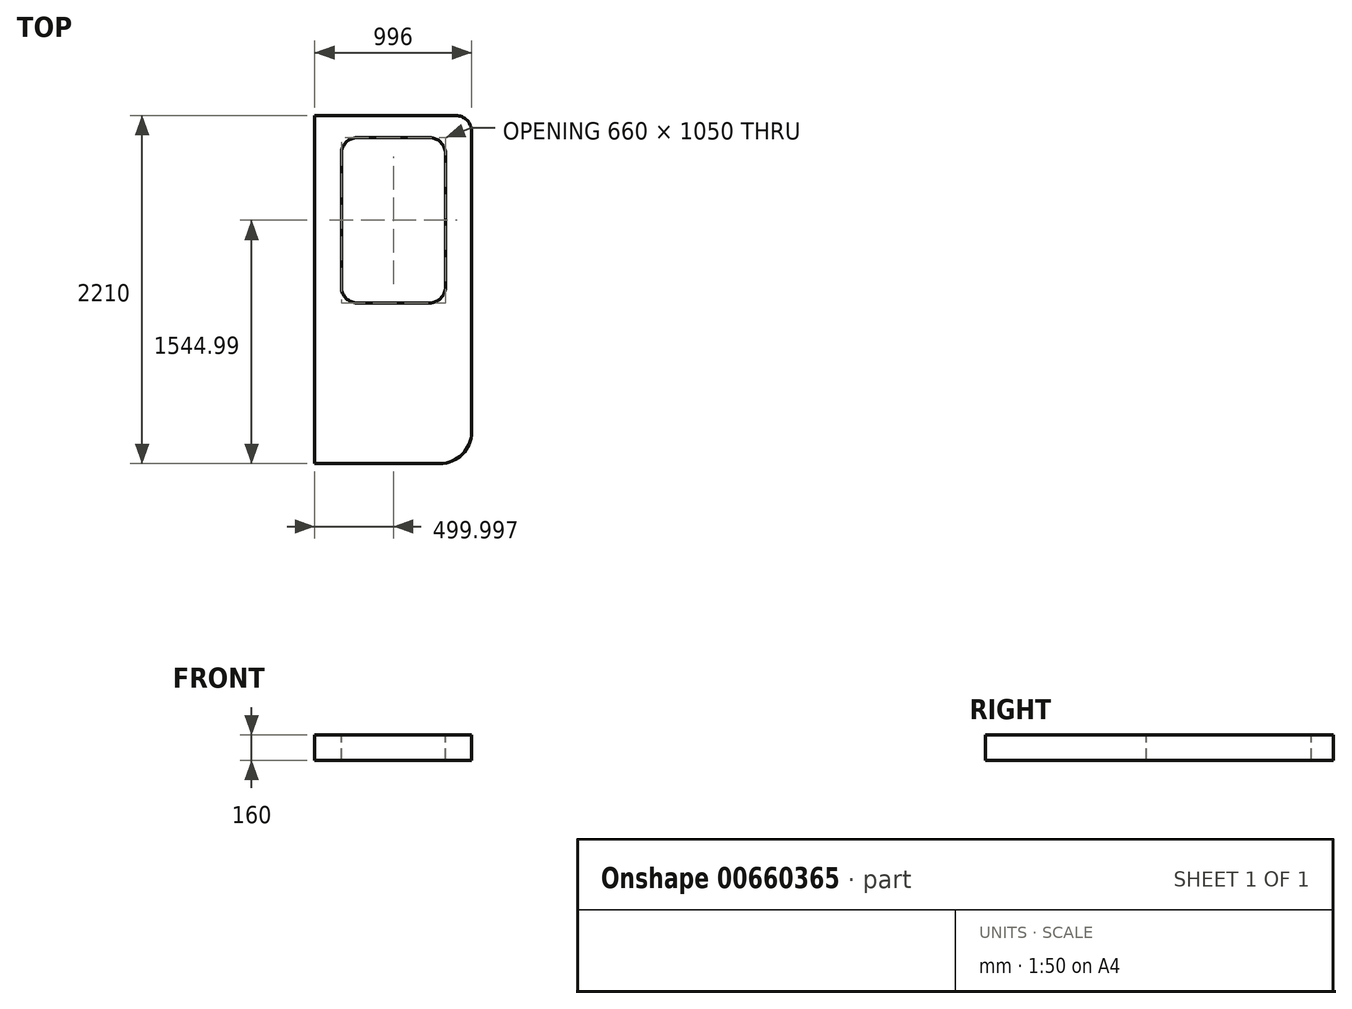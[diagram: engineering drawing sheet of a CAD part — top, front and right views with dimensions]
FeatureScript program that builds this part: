
annotation { "Feature Type Name" : "Feature", "Feature Type Description" : "" }
export const myFeature = defineFeature(function(context is Context, id is Id, definition is map)
    precondition{}
    {
        {
            var Q0;
            Q0=qCreatedBy(makeId("Top.planeOp"),FACE);
            var sketch = newSketch(context, id + "F0", { "sketchPlane" : qUnion([Q0])});
            skLineSegment(sketch, "E0.bottom", {"start": v(-58, 2153.08) * mm, "end": v(938, 2153.08) * mm});
            skLineSegment(sketch, "E0.top", {"start": v(-58, -56.92) * mm, "end": v(938, -56.92) * mm});
            skLineSegment(sketch, "E0.left", {"start": v(-58, 2153.08) * mm, "end": v(-58, -56.92) * mm});
            skLineSegment(sketch, "E0.right", {"start": v(938, 2153.08) * mm, "end": v(938, -56.92) * mm});
            skSolve(sketch);
        }
        {
            var Q0;
            Q0=makeQuery(id+"F0.imprint","IMPRINT",FACE,{"disambiguationData":[TD([[makeQuery(id+"F0.imprint","IMPRINT",EDGE,{"derivedFrom":sQuery(id+"F0.wireOp",EDGE,"E0.bottom")}),-1.0]])]});
            extrude(context, id + "F1", {"entities" : qUnion([Q0]), "depth" : 160 * mm, "offsetDistance" : 25 * mm});
        }
        {
            var Q0;
            Q0=makeQuery(id+"F1.opExtrude","SWEPT_EDGE",EDGE,{"disambiguationData":[OSD([sQuery(id+"F0.wireOp",EDGE,"E0.bottom"),sQuery(id+"F0.wireOp",EDGE,"E0.right")])]});
            fillet(context, id + "F2", {"entities" : qUnion([Q0]), "radius" : 100 * mm, "tangentPropagation" : true, "allowEdgeOverflow" : false});
        }
        {
            var Q0;
            Q0=makeQuery(id+"F1.opExtrude","SWEPT_EDGE",EDGE,{"disambiguationData":[OSD([sQuery(id+"F0.wireOp",EDGE,"E0.top"),sQuery(id+"F0.wireOp",EDGE,"E0.right")])]});
            fillet(context, id + "F3", {"entities" : qUnion([Q0]), "radius" : 200 * mm, "tangentPropagation" : true, "allowEdgeOverflow" : false});
        }
        {
            var Q0;
            Q0=makeQuery(id+"F1.opExtrude","CAP_FACE",FACE,{"disambiguationData":[OSD([sQuery(id+"F0.wireOp",EDGE,"E0.bottom"),sQuery(id+"F0.wireOp",EDGE,"E0.top"),sQuery(id+"F0.wireOp",EDGE,"E0.left"),sQuery(id+"F0.wireOp",EDGE,"E0.right")])],"isStart":false});
            var sketch = newSketch(context, id + "F4", { "sketchPlane" : qUnion([Q0])});
            skLineSegment(sketch, "E1.bottom", {"start": v(212, 2013.08) * mm, "end": v(672, 2013.08) * mm});
            skLineSegment(sketch, "E1.top", {"start": v(212, 963.08) * mm, "end": v(672, 963.08) * mm});
            skLineSegment(sketch, "E1.left", {"start": v(112, 1913.08) * mm, "end": v(112, 1063.08) * mm});
            skLineSegment(sketch, "E1.right", {"start": v(772, 1913.08) * mm, "end": v(772, 1063.08) * mm});
            skPoint(sketch, "E2.visualSharp", {"position": v(772, 2013.08) * mm});
            skArc(sketch, "E2.filletArc", {"start": v(772, 1913.08) * mm, "mid": v(742.72, 1983.79) * mm, "end": v(672, 2013.08) * mm});
            skPoint(sketch, "E3.visualSharp", {"position": v(112, 2013.08) * mm});
            skArc(sketch, "E3.filletArc", {"start": v(212, 2013.08) * mm, "mid": v(141.3, 1983.79) * mm, "end": v(112, 1913.08) * mm});
            skPoint(sketch, "E4.visualSharp", {"position": v(112, 963.08) * mm});
            skArc(sketch, "E4.filletArc", {"start": v(112, 1063.08) * mm, "mid": v(141.3, 992.36) * mm, "end": v(212, 963.08) * mm});
            skPoint(sketch, "E5.visualSharp", {"position": v(772, 963.08) * mm});
            skArc(sketch, "E5.filletArc", {"start": v(672, 963.08) * mm, "mid": v(742.72, 992.36) * mm, "end": v(772, 1063.08) * mm});
            skSolve(sketch);
        }
        {
            var Q0;
            Q0=makeQuery(id+"F4.imprint","IMPRINT",FACE,{"disambiguationData":[TD([[makeQuery(id+"F4.imprint","IMPRINT",EDGE,{"derivedFrom":sQuery(id+"F4.wireOp",EDGE,"E1.bottom")}),-1.0]])]});
            extrude(context, id + "F5", {"entities" : qUnion([Q0]), "operationType" : NewBodyOperationType.REMOVE, "endBound" : BoundingType.UP_TO_NEXT, "oppositeDirection" : true, "depth" : 25 * mm, "offsetDistance" : 25 * mm});
        }
    });
